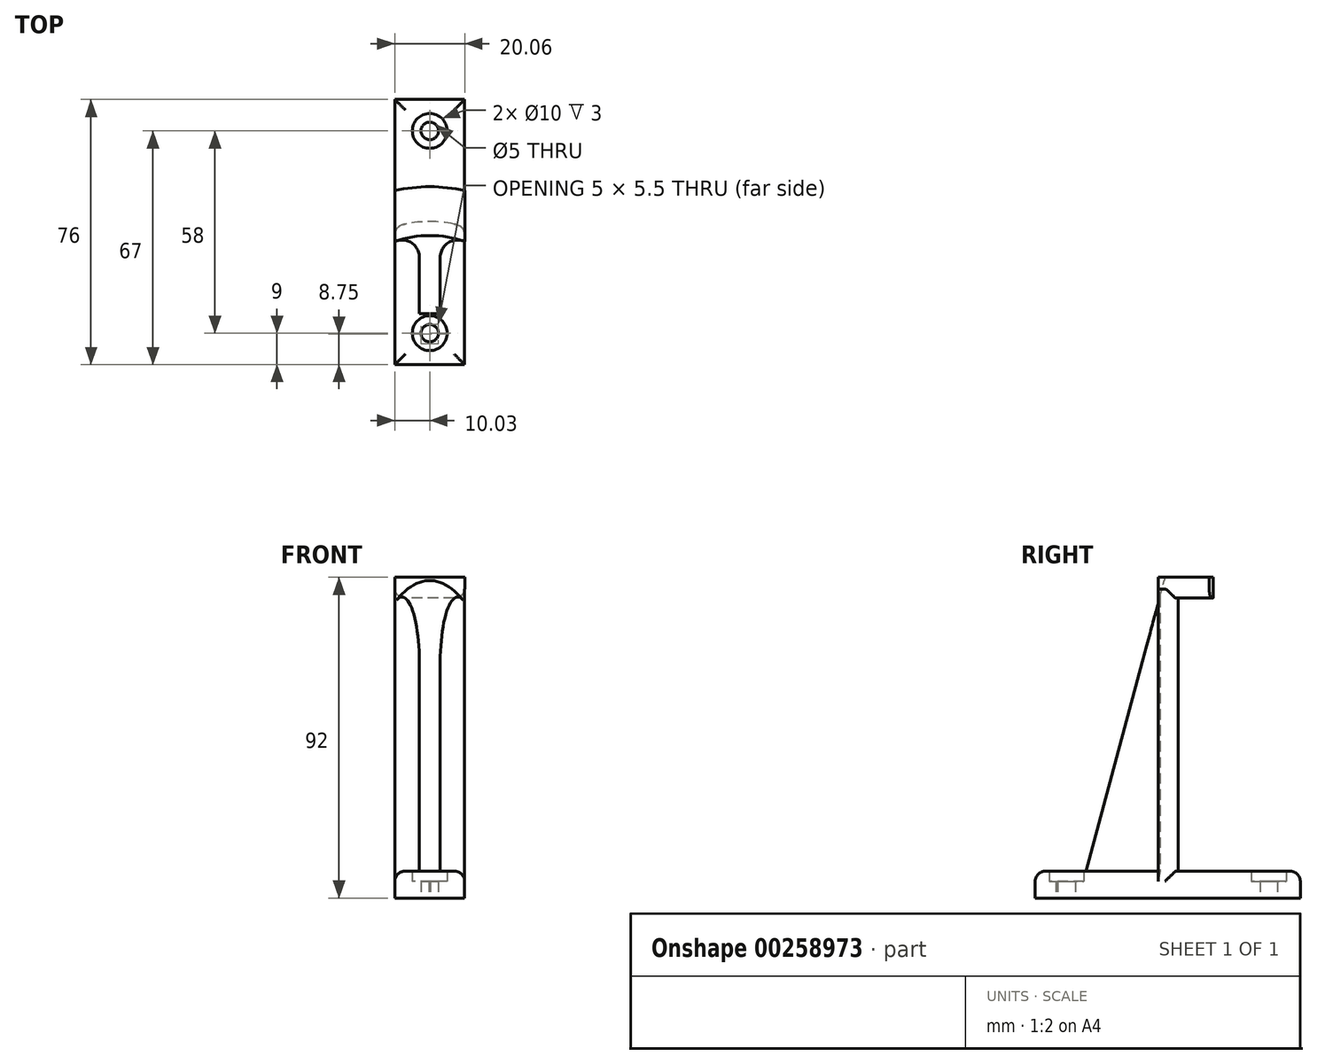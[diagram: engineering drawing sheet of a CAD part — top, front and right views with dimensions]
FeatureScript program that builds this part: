
annotation { "Feature Type Name" : "Feature", "Feature Type Description" : "" }
export const myFeature = defineFeature(function(context is Context, id is Id, definition is map)
    precondition{}
    {
        {
            var Q0;
            Q0=qCreatedBy(makeId("Top.planeOp"),FACE);
            var sketch = newSketch(context, id + "F0", { "sketchPlane" : qUnion([Q0])});
            skCircle(sketch, "E0", {"center": v(0, 0) * mm, "radius": 35 * mm});
            skCircle(sketch, "E1", {"center": v(0, 0) * mm, "radius": 31 * mm});
            skCircle(sketch, "E2", {"center": v(0, 0) * mm, "radius": 45 * mm});
            skLineSegment(sketch, "E3", {"start": v(0, 0) * mm, "end": v(-15.4, 42.29) * mm});
            skLineSegment(sketch, "E4", {"start": v(0, 0) * mm, "end": v(15.4, 42.29) * mm});
            skLineSegment(sketch, "E5", {"start": v(0, 0) * mm, "end": v(0, 45) * mm});
            skLineSegment(sketch, "E6.bottom", {"start": v(10, 35) * mm, "end": v(-10, 35) * mm});
            skLineSegment(sketch, "E6.top", {"start": v(10, 70) * mm, "end": v(-10, 70) * mm});
            skLineSegment(sketch, "E6.left", {"start": v(10, 35) * mm, "end": v(10, 70) * mm});
            skLineSegment(sketch, "E6.right", {"start": v(-10, 35) * mm, "end": v(-10, 70) * mm});
            skPoint(sketch, "E6.middle", {"position": v(0, 52.5) * mm});
            skCircle(sketch, "E7", {"center": v(0, 61) * mm, "radius": 5 * mm});
            skCircle(sketch, "E8", {"center": v(0, 61) * mm, "radius": 2.5 * mm});
            skLineSegment(sketch, "E9.bottom", {"start": v(10, -6) * mm, "end": v(-10, -6) * mm});
            skLineSegment(sketch, "E9.left", {"start": v(10, -6) * mm, "end": v(10, 35) * mm});
            skLineSegment(sketch, "E9.right", {"start": v(-10, -6) * mm, "end": v(-10, 35) * mm});
            skPoint(sketch, "E9.middle", {"position": v(0, 14.5) * mm});
            skCircle(sketch, "E10", {"center": v(0, 3) * mm, "radius": 2.5 * mm});
            skCircle(sketch, "E11", {"center": v(0, 3) * mm, "radius": 5 * mm});
            skSolve(sketch);
        }
        {
            var Q0;
            {var subQ0=sQuery(id+"F0.wireOp",EDGE,"E5");var subQ1=sQuery(id+"F0.wireOp",EDGE,"E0");var subQ2=makeQuery(id+"F0.imprint","INTERSECT",VERTEX,{"derivedFrom":[subQ1,subQ0]});Q0=makeQuery(id+"F0.imprint","IMPRINT",FACE,{"disambiguationData":[TD([[makeQuery(id+"F0.imprint","IMPRINT",EDGE,{"disambiguationData":[TD([[subQ2,1.0]])],"derivedFrom":subQ1}),1.0]])]});}
            var Q1;
            {var subQ0=sQuery(id+"F0.wireOp",EDGE,"E5");var subQ1=sQuery(id+"F0.wireOp",EDGE,"E0");var subQ2=makeQuery(id+"F0.imprint","INTERSECT",VERTEX,{"derivedFrom":[subQ1,subQ0]});Q1=makeQuery(id+"F0.imprint","IMPRINT",FACE,{"disambiguationData":[TD([[makeQuery(id+"F0.imprint","IMPRINT",EDGE,{"disambiguationData":[TD([[subQ2,-1.0]])],"derivedFrom":subQ1}),1.0]])]});}
            extrude(context, id + "F1", {"entities" : qUnion([Q0, Q1]), "depth" : 86 * mm});
        }
        {
            var Q0;
            {var subQ1=sQuery(id+"F0.wireOp",EDGE,"E6.top");Q0=makeQuery(id+"F0.imprint","IMPRINT",FACE,{"disambiguationData":[TD([[makeQuery(id+"F0.imprint","IMPRINT",EDGE,{"derivedFrom":subQ1}),1.0]])]});}
            var Q1;
            {var subQ0=sQuery(id+"F0.wireOp",EDGE,"E6.left");var subQ3=sQuery(id+"F0.wireOp",EDGE,"E2");var subQ4=makeQuery(id+"F0.imprint","INTERSECT",VERTEX,{"derivedFrom":[subQ3,subQ0]});Q1=makeQuery(id+"F0.imprint","IMPRINT",FACE,{"disambiguationData":[TD([[makeQuery(id+"F0.imprint","IMPRINT",EDGE,{"disambiguationData":[TD([[subQ4,-1.0]])],"derivedFrom":subQ3}),1.0]])]});}
            var Q2;
            {var subQ0=sQuery(id+"F0.wireOp",EDGE,"E6.right");var subQ7=sQuery(id+"F0.wireOp",EDGE,"E2");var subQ8=makeQuery(id+"F0.imprint","INTERSECT",VERTEX,{"derivedFrom":[subQ7,subQ0]});Q2=makeQuery(id+"F0.imprint","IMPRINT",FACE,{"disambiguationData":[TD([[makeQuery(id+"F0.imprint","IMPRINT",EDGE,{"disambiguationData":[TD([[subQ8,1.0]])],"derivedFrom":subQ7}),1.0]])]});}
            var Q3;
            {var subQ0=sQuery(id+"F0.wireOp",EDGE,"TI2dgXii-1qb5-BShp-2s3b-O6LjYehV9T6b");var subQ1=sQuery(id+"F0.wireOp",EDGE,"E0");var subQ2=makeQuery(id+"F0.imprint","INTERSECT",VERTEX,{"derivedFrom":[subQ1,subQ0]});Q3=makeQuery(id+"F0.imprint","IMPRINT",FACE,{"disambiguationData":[TD([[makeQuery(id+"F0.imprint","IMPRINT",EDGE,{"disambiguationData":[TD([[subQ2,-1.0]])],"derivedFrom":subQ1}),-1.0]])]});}
            var Q4;
            {var subQ0=sQuery(id+"F0.wireOp",EDGE,"7Phw61sN-cOW4-dQUR-ONVQ-3oVi0tRklzDX");var subQ1=sQuery(id+"F0.wireOp",EDGE,"E0");var subQ2=makeQuery(id+"F0.imprint","INTERSECT",VERTEX,{"derivedFrom":[subQ1,subQ0]});Q4=makeQuery(id+"F0.imprint","IMPRINT",FACE,{"disambiguationData":[TD([[makeQuery(id+"F0.imprint","IMPRINT",EDGE,{"disambiguationData":[TD([[subQ2,1.0]])],"derivedFrom":subQ1}),-1.0]])]});}
            var Q5;
            {var subQ0=sQuery(id+"F0.wireOp",EDGE,"E9.bottom");var subQ3=sQuery(id+"F0.wireOp",EDGE,"E9.left");var subQ5=makeQuery(id+"F0.imprint","INTERSECT",VERTEX,{"derivedFrom":[subQ0,subQ3]});Q5=makeQuery(id+"F0.imprint","IMPRINT",FACE,{"disambiguationData":[TD([[makeQuery(id+"F0.imprint","IMPRINT",EDGE,{"disambiguationData":[TD([[subQ5,-1.0]])],"derivedFrom":subQ3}),1.0]])]});}
            var Q6;
            {var subQ0=sQuery(id+"F0.wireOp",EDGE,"E9.bottom");var subQ3=sQuery(id+"F0.wireOp",EDGE,"E9.right");var subQ5=makeQuery(id+"F0.imprint","INTERSECT",VERTEX,{"derivedFrom":[subQ0,subQ3]});Q6=makeQuery(id+"F0.imprint","IMPRINT",FACE,{"disambiguationData":[TD([[makeQuery(id+"F0.imprint","IMPRINT",EDGE,{"disambiguationData":[TD([[subQ5,-1.0]])],"derivedFrom":subQ3}),-1.0]])]});}
            var Q7;
            {var subQ0=sQuery(id+"F0.wireOp",EDGE,"E5");var subQ1=sQuery(id+"F0.wireOp",EDGE,"E1");var subQ2=makeQuery(id+"F0.imprint","INTERSECT",VERTEX,{"derivedFrom":[subQ1,subQ0]});Q7=makeQuery(id+"F0.imprint","IMPRINT",FACE,{"disambiguationData":[TD([[makeQuery(id+"F0.imprint","IMPRINT",EDGE,{"disambiguationData":[TD([[subQ2,-1.0]])],"derivedFrom":subQ1}),1.0]])]});}
            var Q8;
            {var subQ0=sQuery(id+"F0.wireOp",EDGE,"E9.left");var subQ1=sQuery(id+"F0.wireOp",EDGE,"E1");var subQ2=makeQuery(id+"F0.imprint","INTERSECT",VERTEX,{"derivedFrom":[subQ1,subQ0]});Q8=makeQuery(id+"F0.imprint","IMPRINT",FACE,{"disambiguationData":[TD([[makeQuery(id+"F0.imprint","IMPRINT",EDGE,{"disambiguationData":[TD([[subQ2,-1.0]])],"derivedFrom":subQ1}),1.0]])]});}
            var Q9;
            {var subQ0=sQuery(id+"F0.wireOp",EDGE,"E9.left");var subQ1=sQuery(id+"F0.wireOp",EDGE,"E0");var subQ2=makeQuery(id+"F0.imprint","INTERSECT",VERTEX,{"derivedFrom":[subQ1,subQ0]});Q9=makeQuery(id+"F0.imprint","IMPRINT",FACE,{"disambiguationData":[TD([[makeQuery(id+"F0.imprint","IMPRINT",EDGE,{"disambiguationData":[TD([[subQ2,-1.0]])],"derivedFrom":subQ1}),-1.0]])]});}
            var Q10;
            {var subQ0=sQuery(id+"F0.wireOp",EDGE,"E9.right");var subQ1=sQuery(id+"F0.wireOp",EDGE,"E0");var subQ2=makeQuery(id+"F0.imprint","INTERSECT",VERTEX,{"derivedFrom":[subQ1,subQ0]});Q10=makeQuery(id+"F0.imprint","IMPRINT",FACE,{"disambiguationData":[TD([[makeQuery(id+"F0.imprint","IMPRINT",EDGE,{"disambiguationData":[TD([[subQ2,1.0]])],"derivedFrom":subQ1}),-1.0]])]});}
            extrude(context, id + "F2", {"entities" : qUnion([Q0, Q1, Q2, Q3, Q4, Q5, Q6, Q7, Q8, Q9, Q10]), "operationType" : NewBodyOperationType.ADD, "depth" : 7.75 * mm});
        }
        {
            var Q0;
            Q0=qCreatedBy(makeId("Top.planeOp"),FACE);
            cPlane(context, id + "F3", {"entities" : qUnion([Q0]), "cplaneType" : CPlaneType.OFFSET, "offset" : 83 * mm, "width" : 150 * mm, "height" : 150 * mm});
        }
        {
            var Q0;
            Q0=qCreatedBy(id+"F3.planeOp",FACE);
            var sketch = newSketch(context, id + "F4", { "sketchPlane" : qUnion([Q0])});
            skCircle(sketch, "E12", {"center": v(0, 0) * mm, "radius": 31 * mm});
            skCircle(sketch, "E13", {"center": v(0, 0) * mm, "radius": 35 * mm});
            skCircle(sketch, "E14", {"center": v(0, 0) * mm, "radius": 45 * mm});
            skLineSegment(sketch, "E15", {"start": v(0, 0) * mm, "end": v(0, 45) * mm});
            skLineSegment(sketch, "E16", {"start": v(0, 0) * mm, "end": v(-15.4, 42.29) * mm});
            skLineSegment(sketch, "E17", {"start": v(0, 0) * mm, "end": v(15.4, 42.29) * mm});
            skLineSegment(sketch, "E18", {"start": v(10.03, 27.55) * mm, "end": v(10.03, 33.53) * mm});
            skLineSegment(sketch, "E19.MirrorCS", {"start": v(-10.03, 27.55) * mm, "end": v(-10.03, 33.53) * mm});
            skLineSegment(sketch, "E20", {"start": v(10.03, 33.53) * mm, "end": v(10.03, 43.87) * mm});
            skLineSegment(sketch, "E21.MirrorCS", {"start": v(-10.03, 33.53) * mm, "end": v(-10.03, 43.87) * mm});
            skSolve(sketch);
        }
        {
            var Q0;
            {var subQ0=sQuery(id+"F4.wireOp",EDGE,"E15");var subQ1=sQuery(id+"F4.wireOp",EDGE,"E12");var subQ2=makeQuery(id+"F4.imprint","INTERSECT",VERTEX,{"derivedFrom":[subQ1,subQ0]});Q0=makeQuery(id+"F4.imprint","IMPRINT",FACE,{"disambiguationData":[TD([[makeQuery(id+"F4.imprint","IMPRINT",EDGE,{"disambiguationData":[TD([[subQ2,1.0]])],"derivedFrom":subQ1}),-1.0]])]});}
            var Q1;
            {var subQ0=sQuery(id+"F4.wireOp",EDGE,"E15");var subQ1=sQuery(id+"F4.wireOp",EDGE,"E12");var subQ2=makeQuery(id+"F4.imprint","INTERSECT",VERTEX,{"derivedFrom":[subQ1,subQ0]});Q1=makeQuery(id+"F4.imprint","IMPRINT",FACE,{"disambiguationData":[TD([[makeQuery(id+"F4.imprint","IMPRINT",EDGE,{"disambiguationData":[TD([[subQ2,-1.0]])],"derivedFrom":subQ1}),-1.0]])]});}
            var Q2;
            {var subQ0=sQuery(id+"F4.wireOp",EDGE,"E15");var subQ1=sQuery(id+"F4.wireOp",EDGE,"E13");var subQ2=makeQuery(id+"F4.imprint","INTERSECT",VERTEX,{"derivedFrom":[subQ1,subQ0]});Q2=makeQuery(id+"F4.imprint","IMPRINT",FACE,{"disambiguationData":[TD([[makeQuery(id+"F4.imprint","IMPRINT",EDGE,{"disambiguationData":[TD([[subQ2,1.0]])],"derivedFrom":subQ1}),-1.0]])]});}
            var Q3;
            {var subQ0=sQuery(id+"F4.wireOp",EDGE,"E15");var subQ1=sQuery(id+"F4.wireOp",EDGE,"E13");var subQ2=makeQuery(id+"F4.imprint","INTERSECT",VERTEX,{"derivedFrom":[subQ1,subQ0]});Q3=makeQuery(id+"F4.imprint","IMPRINT",FACE,{"disambiguationData":[TD([[makeQuery(id+"F4.imprint","IMPRINT",EDGE,{"disambiguationData":[TD([[subQ2,-1.0]])],"derivedFrom":subQ1}),-1.0]])]});}
            extrude(context, id + "F5", {"entities" : qUnion([Q0, Q1, Q2, Q3]), "operationType" : NewBodyOperationType.ADD, "depth" : 9 * mm, "hasSecondDirection" : true, "secondDirectionOppositeDirection" : false, "secondDirectionDepth" : 3 * mm});
        }
        {
            var Q0;
            {var subQ0=sQuery(id+"F0.wireOp",EDGE,"E5");var subQ1=sQuery(id+"F0.wireOp",EDGE,"E2");var subQ2=makeQuery(id+"F0.imprint","INTERSECT",VERTEX,{"derivedFrom":[subQ1,subQ0]});Q0=makeQuery(id+"F0.imprint","IMPRINT",FACE,{"disambiguationData":[TD([[makeQuery(id+"F0.imprint","IMPRINT",EDGE,{"disambiguationData":[TD([[subQ2,1.0]])],"derivedFrom":subQ1}),1.0]])]});}
            var Q1;
            {var subQ0=sQuery(id+"F0.wireOp",EDGE,"E5");var subQ1=sQuery(id+"F0.wireOp",EDGE,"E2");var subQ2=makeQuery(id+"F0.imprint","INTERSECT",VERTEX,{"derivedFrom":[subQ1,subQ0]});Q1=makeQuery(id+"F0.imprint","IMPRINT",FACE,{"disambiguationData":[TD([[makeQuery(id+"F0.imprint","IMPRINT",EDGE,{"disambiguationData":[TD([[subQ2,-1.0]])],"derivedFrom":subQ1}),1.0]])]});}
            var Q2;
            Q2=makeQuery(id+"F0.imprint","IMPRINT",FACE,{"disambiguationData":[TD([[makeQuery(id+"F0.imprint","IMPRINT",EDGE,{"derivedFrom":sQuery(id+"F0.wireOp",EDGE,"E7")}),1.0]])]});
            var Q3;
            {var subQ1=sQuery(id+"F0.wireOp",EDGE,"E6.top");Q3=makeQuery(id+"F0.imprint","IMPRINT",FACE,{"disambiguationData":[TD([[makeQuery(id+"F0.imprint","IMPRINT",EDGE,{"derivedFrom":subQ1}),1.0]])]});}
            var Q4;
            {var subQ0=sQuery(id+"F0.wireOp",EDGE,"E10");var subQ5=sQuery(id+"F0.wireOp",EDGE,"E3");var subQ9=makeQuery(id+"F0.imprint","INTERSECT",VERTEX,{"disambiguationData":[OD(1.0)],"derivedFrom":[subQ5,subQ0]});Q4=makeQuery(id+"F0.imprint","IMPRINT",FACE,{"disambiguationData":[TD([[makeQuery(id+"F0.imprint","IMPRINT",EDGE,{"disambiguationData":[TD([[subQ9,-1.0]])],"derivedFrom":subQ5}),1.0]])]});}
            var Q5;
            {var subQ0=sQuery(id+"F0.wireOp",EDGE,"E10");var subQ1=sQuery(id+"F0.wireOp",EDGE,"E3");var subQ2=makeQuery(id+"F0.imprint","INTERSECT",VERTEX,{"disambiguationData":[OD(1.0)],"derivedFrom":[subQ1,subQ0]});Q5=makeQuery(id+"F0.imprint","IMPRINT",FACE,{"disambiguationData":[TD([[makeQuery(id+"F0.imprint","IMPRINT",EDGE,{"disambiguationData":[TD([[subQ2,-1.0]])],"derivedFrom":subQ1}),-1.0]])]});}
            var Q6;
            {var subQ0=sQuery(id+"F0.wireOp",EDGE,"E10");var subQ1=sQuery(id+"F0.wireOp",EDGE,"E4");var subQ2=makeQuery(id+"F0.imprint","INTERSECT",VERTEX,{"disambiguationData":[OD(1.0)],"derivedFrom":[subQ1,subQ0]});Q6=makeQuery(id+"F0.imprint","IMPRINT",FACE,{"disambiguationData":[TD([[makeQuery(id+"F0.imprint","IMPRINT",EDGE,{"disambiguationData":[TD([[subQ2,-1.0]])],"derivedFrom":subQ1}),1.0]])]});}
            extrude(context, id + "F6", {"entities" : qUnion([Q0, Q1, Q2, Q3, Q4, Q5, Q6]), "operationType" : NewBodyOperationType.ADD, "depth" : 4.75 * mm});
        }
        {
            var Q0;
            Q0=qCreatedBy(makeId("Right.planeOp"),FACE);
            var sketch = newSketch(context, id + "F7", { "sketchPlane" : qUnion([Q0])});
            skLineSegment(sketch, "E22", {"start": v(8.63, 7.75) * mm, "end": v(31.18, 7.75) * mm});
            skLineSegment(sketch, "E23", {"start": v(31.18, 7.75) * mm, "end": v(31.18, 91.75) * mm});
            skLineSegment(sketch, "E24", {"start": v(31.18, 91.75) * mm, "end": v(8.63, 7.75) * mm});
            skSolve(sketch);
        }
        {
            var Q0;
            Q0=makeQuery(id+"F7.imprint","IMPRINT",FACE,{"disambiguationData":[TD([[makeQuery(id+"F7.imprint","IMPRINT",EDGE,{"derivedFrom":sQuery(id+"F7.wireOp",EDGE,"E22")}),1.0]])]});
            extrude(context, id + "F8", {"entities" : qUnion([Q0]), "operationType" : NewBodyOperationType.ADD, "depth" : 3 * mm, "hasSecondDirection" : true, "secondDirectionOppositeDirection" : true, "secondDirectionDepth" : 3 * mm});
        }
        {
            var Q0;
            Q0=makeQuery(id+"F5.opExtrude","CAP_EDGE",EDGE,{"disambiguationData":[OSD([sQuery(id+"F4.wireOp",EDGE,"E19.MirrorCS"),sQuery(id+"F4.wireOp",EDGE,"E21.MirrorCS")])],"isStart":true});
            var Q1;
            Q1=makeQuery(id+"F5.opExtrude","CAP_EDGE",EDGE,{"disambiguationData":[OSD([sQuery(id+"F4.wireOp",EDGE,"E18"),sQuery(id+"F4.wireOp",EDGE,"E20")])],"isStart":true});
            var Q2;
            Q2=makeQuery(id+"F2.opExtrude","CAP_EDGE",EDGE,{"disambiguationData":[OSD([sQuery(id+"F0.wireOp",EDGE,"E6.left"),sQuery(id+"F0.wireOp",EDGE,"E9.left")])],"isStart":false});
            var Q3;
            Q3=makeQuery(id+"F2.opExtrude","CAP_EDGE",EDGE,{"disambiguationData":[OSD([sQuery(id+"F0.wireOp",EDGE,"E6.right"),sQuery(id+"F0.wireOp",EDGE,"E9.right")])],"isStart":false});
            var Q4;
            Q4=makeQuery(id+"F2.opExtrude","CAP_EDGE",EDGE,{"disambiguationData":[OSD([sQuery(id+"F0.wireOp",EDGE,"E9.right")])],"isStart":false});
            var Q5;
            Q5=makeQuery(id+"F2.opExtrude","CAP_EDGE",EDGE,{"disambiguationData":[OSD([sQuery(id+"F0.wireOp",EDGE,"E9.left")])],"isStart":false});
            var Q6;
            Q6=makeQuery(id+"F2.opExtrude","CAP_EDGE",EDGE,{"disambiguationData":[OSD([sQuery(id+"F0.wireOp",EDGE,"E6.top")])],"isStart":false});
            var Q7;
            Q7=makeQuery(id+"F2.opExtrude","CAP_EDGE",EDGE,{"disambiguationData":[OSD([sQuery(id+"F0.wireOp",EDGE,"E9.bottom")])],"isStart":false});
            fillet(context, id + "F9", {"entities" : qUnion([Q0, Q1, Q2, Q3, Q4, Q5, Q6, Q7]), "radius" : 3 * mm, "tangentPropagation" : true, "allowEdgeOverflow" : false});
        }
        {
            var Q0;
            Q0=makeQuery(id+"F1.opExtrude","SWEPT_EDGE",EDGE,{"disambiguationData":[OSD([sQuery(id+"F0.wireOp",EDGE,"E0"),sQuery(id+"F0.wireOp",EDGE,"E9.left")])]});
            var Q1;
            Q1=makeQuery(id+"F1.opExtrude","SWEPT_EDGE",EDGE,{"disambiguationData":[OSD([sQuery(id+"F0.wireOp",EDGE,"E0"),sQuery(id+"F0.wireOp",EDGE,"E9.right")])]});
            fillet(context, id + "F10", {"entities" : qUnion([Q0, Q1]), "radius" : 3 * mm, "tangentPropagation" : true, "allowEdgeOverflow" : false});
        }
        {
            var Q0;
            Q0=makeQuery(id+"F8.opExtrude","CAP_EDGE",EDGE,{"disambiguationData":[OSD([sQuery(id+"F7.wireOp",EDGE,"E22")])],"isStart":false});
            var Q1;
            Q1=makeQuery(id+"F8.opExtrude","CAP_EDGE",EDGE,{"disambiguationData":[OSD([sQuery(id+"F7.wireOp",EDGE,"E22")])],"isStart":true});
            var Q2;
            Q2=makeQuery(id+"F8.opExtrude","SWEPT_EDGE",EDGE,{"disambiguationData":[OSD([sQuery(id+"F7.wireOp",EDGE,"E22"),sQuery(id+"F7.wireOp",EDGE,"E24")])]});
            var Q3;
            Q3=makeQuery(id+"F2.opExtrude","CAP_EDGE",EDGE,{"disambiguationData":[OSD([sQuery(id+"F0.wireOp",EDGE,"E0")])],"isStart":false});
            var Q4;
            Q4=makeQuery(id+"F8.boolean.opBoolean","INTERSECT",EDGE,{"derivedFrom":[makeQuery(id+"F5.boolean.opBoolean","MERGE",FACE,{"derivedFrom":[makeQuery(id+"F1.opExtrude","SWEPT_FACE",FACE,{"disambiguationData":[OSD([sQuery(id+"F0.wireOp",EDGE,"E1")])]}),makeQuery(id+"F5.opExtrude","SWEPT_FACE",FACE,{"disambiguationData":[OSD([sQuery(id+"F4.wireOp",EDGE,"E12")])]})]}),makeQuery(id+"F8.opExtrude","CAP_FACE",FACE,{"disambiguationData":[OSD([sQuery(id+"F7.wireOp",EDGE,"E22"),sQuery(id+"F7.wireOp",EDGE,"E23"),sQuery(id+"F7.wireOp",EDGE,"E24")])],"isStart":false})]});
            var Q5;
            Q5=makeQuery(id+"F8.boolean.opBoolean","INTERSECT",EDGE,{"derivedFrom":[makeQuery(id+"F5.boolean.opBoolean","MERGE",FACE,{"derivedFrom":[makeQuery(id+"F1.opExtrude","SWEPT_FACE",FACE,{"disambiguationData":[OSD([sQuery(id+"F0.wireOp",EDGE,"E1")])]}),makeQuery(id+"F5.opExtrude","SWEPT_FACE",FACE,{"disambiguationData":[OSD([sQuery(id+"F4.wireOp",EDGE,"E12")])]})]}),makeQuery(id+"F8.opExtrude","CAP_FACE",FACE,{"disambiguationData":[OSD([sQuery(id+"F7.wireOp",EDGE,"E22"),sQuery(id+"F7.wireOp",EDGE,"E23"),sQuery(id+"F7.wireOp",EDGE,"E24")])],"isStart":true})]});
            fillet(context, id + "F11", {"entities" : qUnion([Q0, Q1, Q2, Q3, Q4, Q5]), "radius" : 5 * mm, "tangentPropagation" : true, "allowEdgeOverflow" : false});
        }
    });
